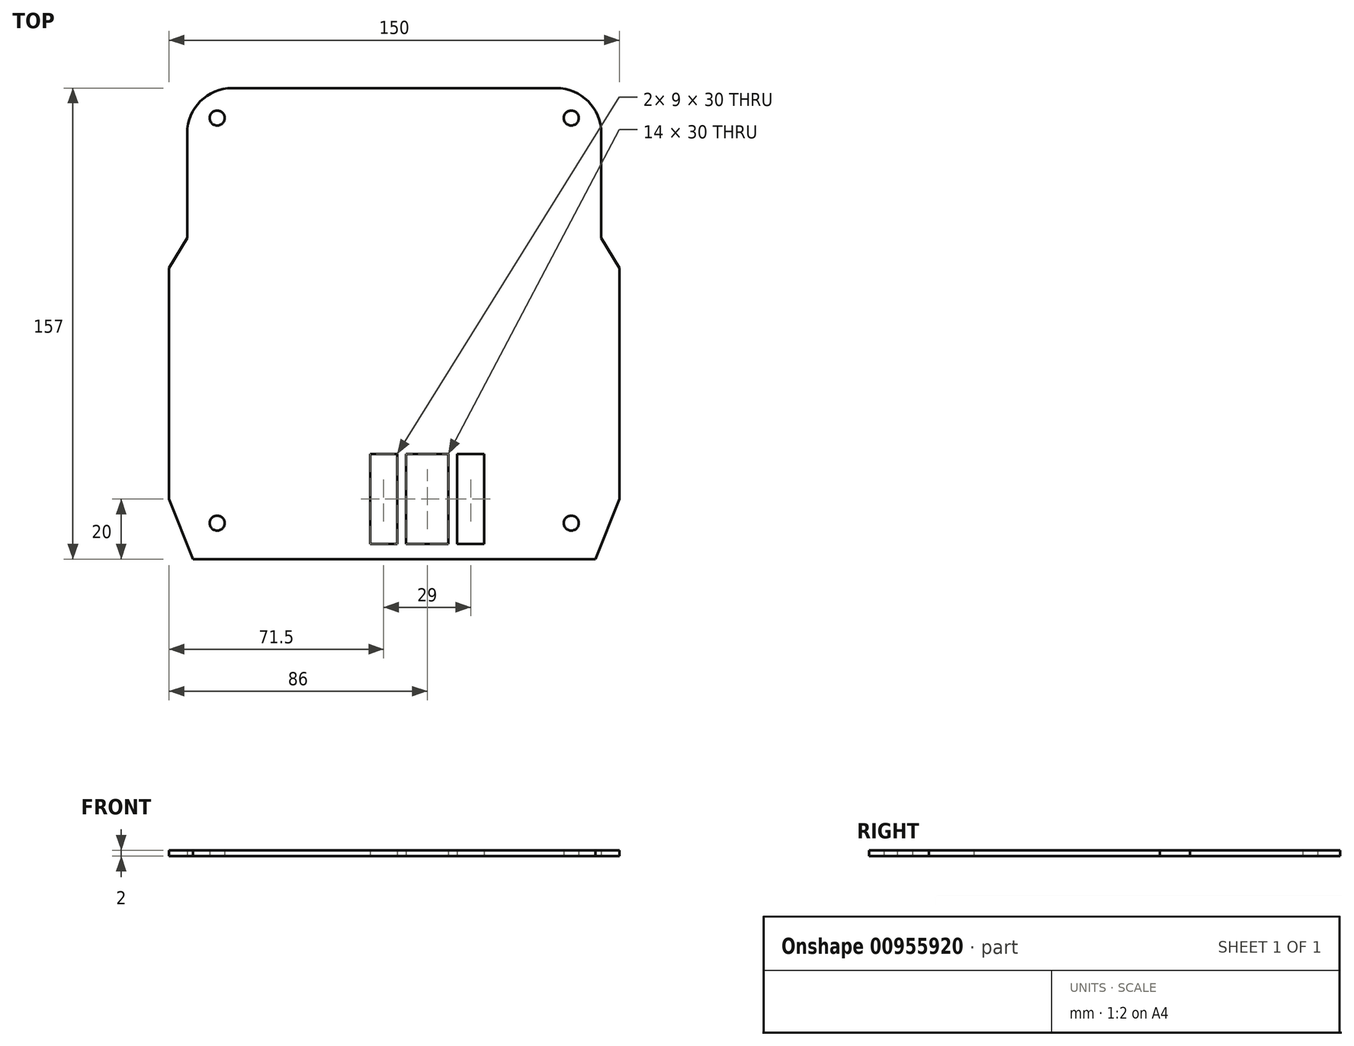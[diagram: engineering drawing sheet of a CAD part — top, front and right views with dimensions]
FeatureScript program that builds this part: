
annotation { "Feature Type Name" : "Feature", "Feature Type Description" : "" }
export const myFeature = defineFeature(function(context is Context, id is Id, definition is map)
    precondition{}
    {
        {
            var Q0;
            Q0=qCreatedBy(makeId("Top.planeOp"),FACE);
            var sketch = newSketch(context, id + "F0", { "sketchPlane" : qUnion([Q0])});
            skCircle(sketch, "E0", {"center": v(-59, 0) * mm, "radius": 2.5 * mm});
            skCircle(sketch, "E1", {"center": v(-59, -135) * mm, "radius": 2.5 * mm});
            skLineSegment(sketch, "E2", {"start": v(0, 10) * mm, "end": v(-54, 10) * mm});
            skLineSegment(sketch, "E3", {"start": v(-69, -5) * mm, "end": v(-69, -40) * mm});
            skLineSegment(sketch, "E4", {"start": v(-75, -50) * mm, "end": v(-75, -127) * mm});
            skLineSegment(sketch, "E5", {"start": v(-75, -50) * mm, "end": v(-69, -40) * mm});
            skLineSegment(sketch, "E6", {"start": v(-67, -147) * mm, "end": v(0, -147) * mm});
            skLineSegment(sketch, "E7", {"start": v(-75, -127) * mm, "end": v(-67, -147) * mm});
            skPoint(sketch, "E8.visualSharp", {"position": v(-69, 10) * mm});
            skArc(sketch, "E8.filletArc", {"start": v(-54, 10) * mm, "mid": v(-64.6, 5.6) * mm, "end": v(-69, -5) * mm});
            skLineSegment(sketch, "E9.MirrorCS", {"start": v(0, 10) * mm, "end": v(54, 10) * mm});
            skPoint(sketch, "E10.MirrorP", {"position": v(69, 10) * mm});
            skArc(sketch, "E11.MirrorCS", {"start": v(54, 10) * mm, "mid": v(64.6, 5.6) * mm, "end": v(69, -5) * mm});
            skLineSegment(sketch, "E12.MirrorCS", {"start": v(69, -5) * mm, "end": v(69, -40) * mm});
            skLineSegment(sketch, "E13.MirrorCS", {"start": v(75, -50) * mm, "end": v(69, -40) * mm});
            skLineSegment(sketch, "E14.MirrorCS", {"start": v(75, -50) * mm, "end": v(75, -127) * mm});
            skLineSegment(sketch, "E15.MirrorCS", {"start": v(75, -127) * mm, "end": v(67, -147) * mm});
            skLineSegment(sketch, "E16.MirrorCS", {"start": v(67, -147) * mm, "end": v(0, -147) * mm});
            skCircle(sketch, "E17.MirrorC", {"center": v(59, -135) * mm, "radius": 2.5 * mm});
            skCircle(sketch, "E18.MirrorC", {"center": v(59, 0) * mm, "radius": 2.5 * mm});
            skLineSegment(sketch, "E19", {"start": v(30, -142) * mm, "end": v(30, -112) * mm});
            skLineSegment(sketch, "E20", {"start": v(30, -112) * mm, "end": v(-8, -112) * mm});
            skLineSegment(sketch, "E21", {"start": v(-8, -112) * mm, "end": v(-8, -142) * mm});
            skLineSegment(sketch, "E22", {"start": v(-8, -142) * mm, "end": v(30, -142) * mm});
            skLineSegment(sketch, "E23", {"start": v(1, -112) * mm, "end": v(1, -142) * mm});
            skLineSegment(sketch, "E24", {"start": v(4, -112) * mm, "end": v(4, -142) * mm});
            skLineSegment(sketch, "E25", {"start": v(11, -112) * mm, "end": v(11, -142) * mm, "construction": true});
            skLineSegment(sketch, "E26.MirrorCS", {"start": v(18, -112) * mm, "end": v(18, -142) * mm});
            skLineSegment(sketch, "E27.MirrorCS", {"start": v(21, -112) * mm, "end": v(21, -142) * mm});
            skSolve(sketch);
        }
        {
            var Q0;
            Q0=makeQuery(id+"F0.imprint","IMPRINT",FACE,{"disambiguationData":[TD([[makeQuery(id+"F0.imprint","IMPRINT",EDGE,{"derivedFrom":sQuery(id+"F0.wireOp",EDGE,"E0")}),-1.0]])]});
            var Q1;
            {var subQ0=sQuery(id+"F0.wireOp",EDGE,"E23");Q1=makeQuery(id+"F0.imprint","IMPRINT",FACE,{"disambiguationData":[TD([[makeQuery(id+"F0.imprint","IMPRINT",EDGE,{"derivedFrom":subQ0}),1.0]])]});}
            var Q2;
            {var subQ0=sQuery(id+"F0.wireOp",EDGE,"E26.MirrorCS");Q2=makeQuery(id+"F0.imprint","IMPRINT",FACE,{"disambiguationData":[TD([[makeQuery(id+"F0.imprint","IMPRINT",EDGE,{"derivedFrom":subQ0}),1.0]])]});}
            extrude(context, id + "F1", {"entities" : qUnion([Q0, Q1, Q2]), "depth" : 2 * mm, "offsetDistance" : 25 * mm});
        }
    });
